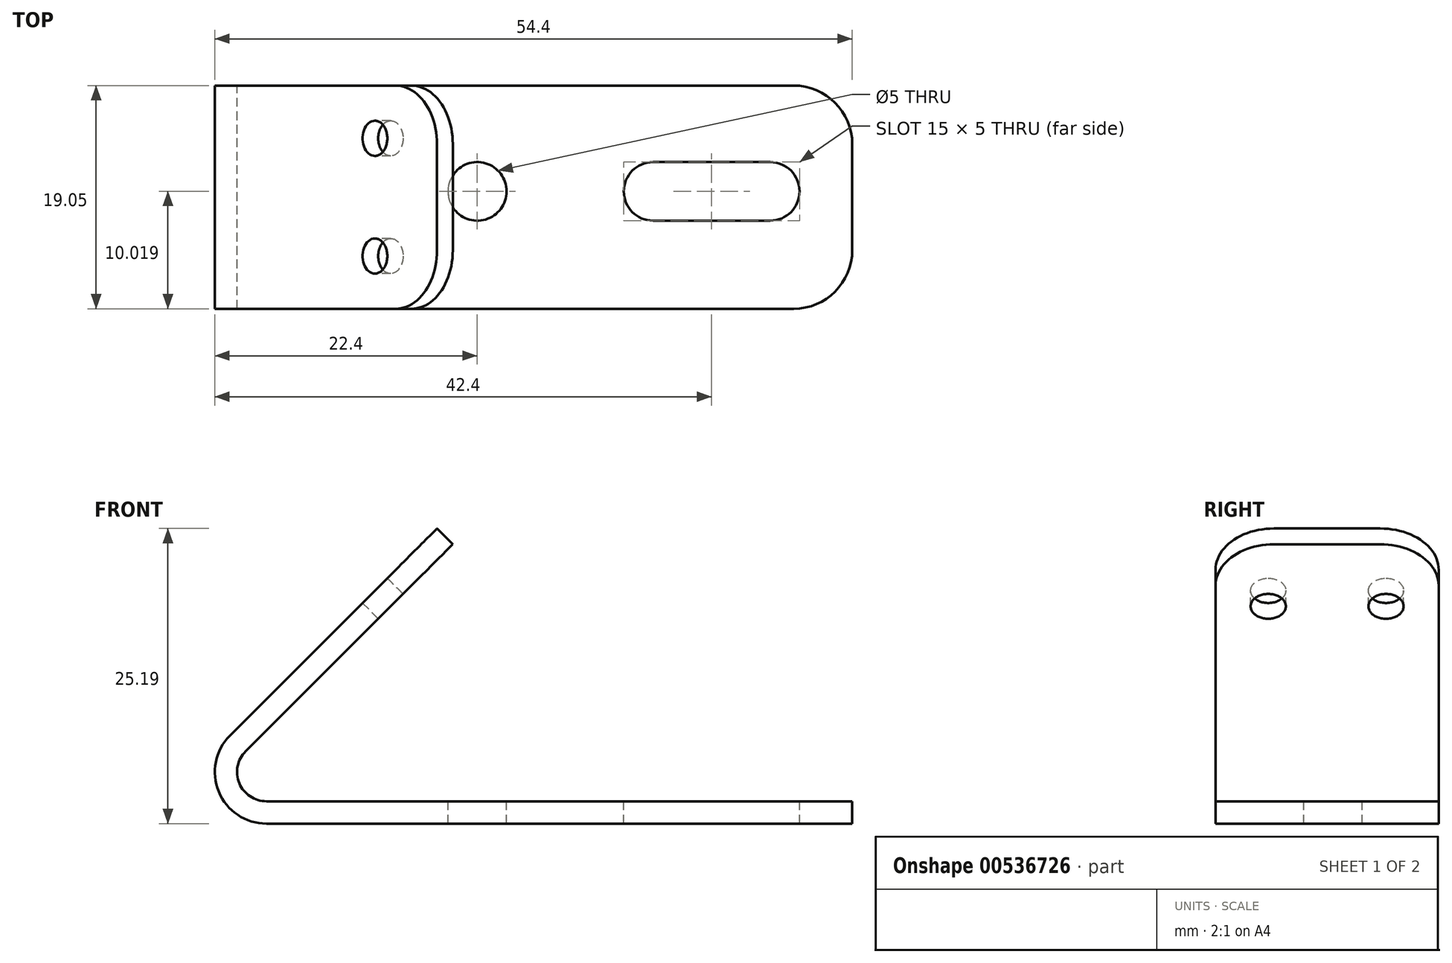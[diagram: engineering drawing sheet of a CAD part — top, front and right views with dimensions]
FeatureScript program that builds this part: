
annotation { "Feature Type Name" : "Feature", "Feature Type Description" : "" }
export const myFeature = defineFeature(function(context is Context, id is Id, definition is map)
    precondition{}
    {
        {
            var Q0;
            Q0=qCreatedBy(makeId("Front.planeOp"),FACE);
            var sketch = newSketch(context, id + "F0", { "sketchPlane" : qUnion([Q0])});
            skArc(sketch, "E0", {"start": v(-3.11, 3.11) * mm, "mid": v(-4.07, -1.68) * mm, "end": v(0, -4.4) * mm});
            skLineSegment(sketch, "E1", {"start": v(14.57, 20.79) * mm, "end": v(-3.11, 3.11) * mm});
            skLineSegment(sketch, "E2", {"start": v(0, -4.4) * mm, "end": v(50, -4.4) * mm});
            skLineSegment(sketch, "E3.0", {"start": v(0, -2.5) * mm, "end": v(50, -2.5) * mm});
            skArc(sketch, "E3.1", {"start": v(-1.77, 1.77) * mm, "mid": v(-2.3, -0.96) * mm, "end": v(0, -2.5) * mm});
            skLineSegment(sketch, "E3.2", {"start": v(15.9, 19.45) * mm, "end": v(-1.77, 1.77) * mm});
            skLineSegment(sketch, "E4", {"start": v(14.57, 20.79) * mm, "end": v(15.9, 19.45) * mm});
            skLineSegment(sketch, "E5", {"start": v(50, -2.5) * mm, "end": v(50, -4.4) * mm});
            skSolve(sketch);
        }
        {
            var Q0;
            Q0 = qSketchRegion(id + "F0", true);
            extrude(context, id + "F1", {"entities" : qUnion([Q0]), "depth" : 19.05 * mm, "offsetDistance" : 25 * mm});
        }
        {
            var Q0;
            Q0=makeQuery(id+"F1.opExtrude","SWEPT_FACE",FACE,{"disambiguationData":[OSD([sQuery(id+"F0.wireOp",EDGE,"E3.0")])]});
            var sketch = newSketch(context, id + "F2", { "sketchPlane" : qUnion([Q0])});
            skCircle(sketch, "E6", {"center": v(18, -9.03) * mm, "radius": 2.5 * mm});
            skLineSegment(sketch, "E7.bottom", {"start": v(43, -11.53) * mm, "end": v(33, -11.53) * mm});
            skLineSegment(sketch, "E7.top", {"start": v(43, -6.53) * mm, "end": v(33, -6.53) * mm});
            skPoint(sketch, "E7.middle", {"position": v(38, -9.03) * mm});
            skArc(sketch, "E8", {"start": v(33, -6.53) * mm, "mid": v(30.5, -9.03) * mm, "end": v(33, -11.53) * mm});
            skArc(sketch, "E9", {"start": v(43, -11.53) * mm, "mid": v(45.5, -9.03) * mm, "end": v(43, -6.53) * mm});
            skSolve(sketch);
        }
        {
            var Q0;
            Q0 = qSketchRegion(id + "F2", true);
            extrude(context, id + "F3", {"entities" : qUnion([Q0]), "operationType" : NewBodyOperationType.REMOVE, "endBound" : BoundingType.THROUGH_ALL, "oppositeDirection" : true, "depth" : 25 * mm, "offsetDistance" : 25 * mm});
        }
        {
            var Q0;
            Q0=makeQuery(id+"F1.opExtrude","CAP_EDGE",EDGE,{"disambiguationData":[OSD([sQuery(id+"F0.wireOp",EDGE,"E5")])],"isStart":false});
            var Q1;
            Q1=makeQuery(id+"F1.opExtrude","CAP_EDGE",EDGE,{"disambiguationData":[OSD([sQuery(id+"F0.wireOp",EDGE,"E5")])],"isStart":true});
            fillet(context, id + "F4", {"entities" : qUnion([Q0, Q1]), "radius" : 5 * mm, "tangentPropagation" : true, "allowEdgeOverflow" : false});
        }
        {
            var Q0;
            Q0=makeQuery(id+"F1.opExtrude","CAP_EDGE",EDGE,{"disambiguationData":[OSD([sQuery(id+"F0.wireOp",EDGE,"E4")])],"isStart":false});
            var Q1;
            Q1=makeQuery(id+"F1.opExtrude","CAP_EDGE",EDGE,{"disambiguationData":[OSD([sQuery(id+"F0.wireOp",EDGE,"E4")])],"isStart":true});
            fillet(context, id + "F5", {"entities" : qUnion([Q0, Q1]), "radius" : 5 * mm, "tangentPropagation" : true, "allowEdgeOverflow" : false});
        }
        {
            var Q0;
            Q0=makeQuery(id+"F1.opExtrude","SWEPT_FACE",FACE,{"disambiguationData":[OSD([sQuery(id+"F0.wireOp",EDGE,"E1")])]});
            var sketch = newSketch(context, id + "F6", { "sketchPlane" : qUnion([Q0])});
            skCircle(sketch, "E10", {"center": v(4.5, 17.5) * mm, "radius": 1.5 * mm});
            skCircle(sketch, "E11", {"center": v(14.55, 17.5) * mm, "radius": 1.5 * mm});
            skSolve(sketch);
        }
        {
            var Q0;
            Q0 = qSketchRegion(id + "F6", true);
            var Q1;
            Q1=makeQuery(id+"F1.opExtrude","SWEPT_FACE",FACE,{"disambiguationData":[OSD([sQuery(id+"F0.wireOp",EDGE,"E3.2")])]});
            extrude(context, id + "F7", {"entities" : qUnion([Q0]), "operationType" : NewBodyOperationType.REMOVE, "endBound" : BoundingType.UP_TO_SURFACE, "oppositeDirection" : true, "depth" : 25 * mm, "endBoundEntityFace" : qUnion([Q1]), "offsetDistance" : 25 * mm});
        }
    });
